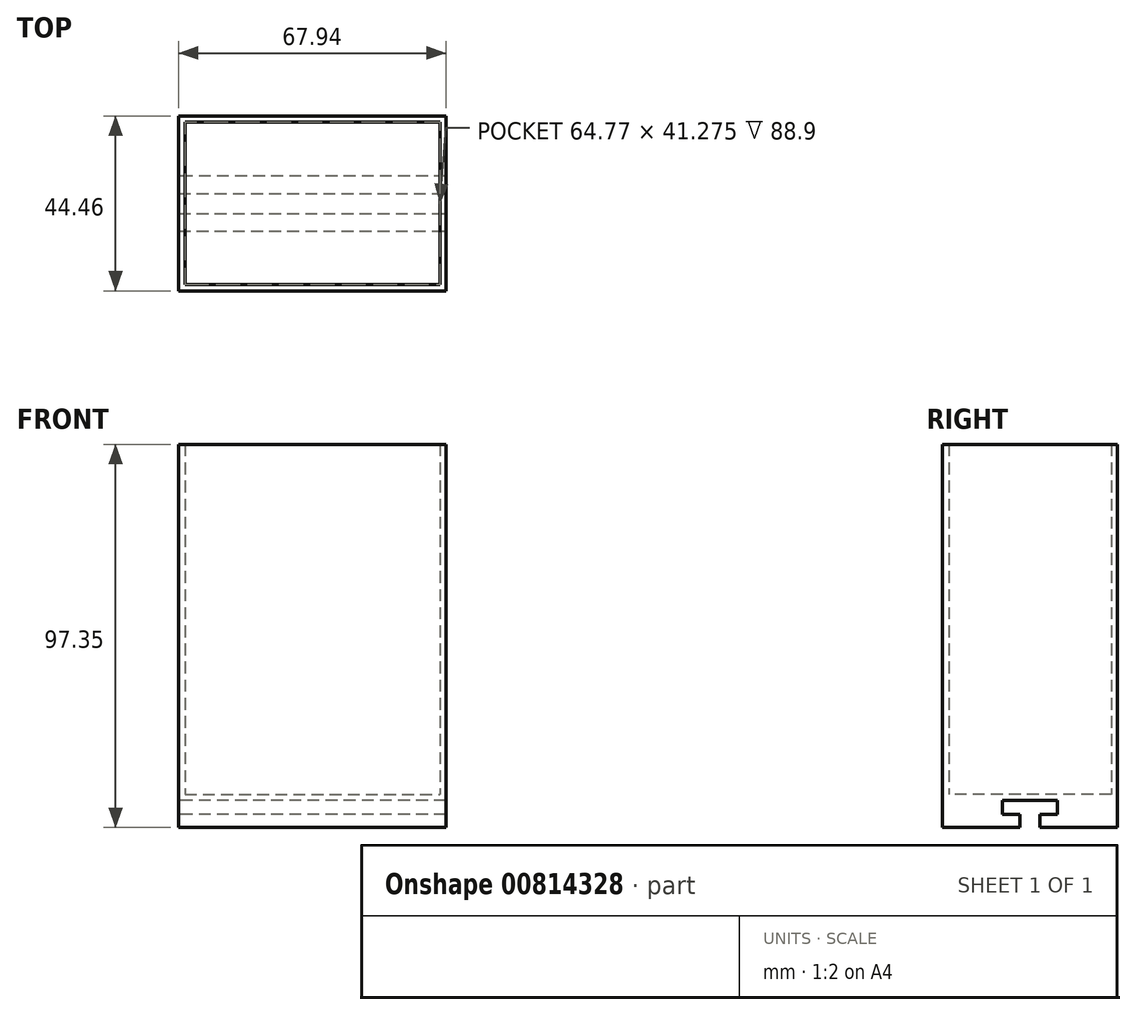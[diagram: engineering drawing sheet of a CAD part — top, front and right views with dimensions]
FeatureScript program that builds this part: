
annotation { "Feature Type Name" : "Feature", "Feature Type Description" : "" }
export const myFeature = defineFeature(function(context is Context, id is Id, definition is map)
    precondition{}
    {
        {
            var Q0;
            Q0=qCreatedBy(makeId("Top.planeOp"),FACE);
            var sketch = newSketch(context, id + "F0", { "sketchPlane" : qUnion([Q0])});
            skLineSegment(sketch, "E0.bottom", {"start": v(-33.97, 22.23) * mm, "end": v(33.97, 22.23) * mm});
            skLineSegment(sketch, "E0.top", {"start": v(-33.97, -22.23) * mm, "end": v(33.97, -22.23) * mm});
            skLineSegment(sketch, "E0.left", {"start": v(-33.97, 22.23) * mm, "end": v(-33.97, -22.23) * mm});
            skLineSegment(sketch, "E0.right", {"start": v(33.97, 22.23) * mm, "end": v(33.97, -22.23) * mm});
            skLineSegment(sketch, "E1", {"start": v(-33.97, 22.23) * mm, "end": v(33.97, -22.23) * mm, "construction": true});
            skSolve(sketch);
        }
        {
            var Q0;
            Q0 = qSketchRegion(id + "F0", true);
            extrude(context, id + "F1", {"entities" : qUnion([Q0]), "depth" : 1.59 * mm, "offsetDistance" : 25.4 * mm});
        }
        {
            var Q0;
            Q0=makeQuery(id+"F1.opExtrude","CAP_FACE",FACE,{"disambiguationData":[OSD([sQuery(id+"F0.wireOp",EDGE,"E0.bottom"),sQuery(id+"F0.wireOp",EDGE,"E0.top"),sQuery(id+"F0.wireOp",EDGE,"E0.left"),sQuery(id+"F0.wireOp",EDGE,"E0.right")])],"isStart":false});
            var sketch = newSketch(context, id + "F2", { "sketchPlane" : qUnion([Q0])});
            skLineSegment(sketch, "E2.bottom", {"start": v(-33.97, 22.23) * mm, "end": v(33.97, 22.23) * mm});
            skLineSegment(sketch, "E2.top", {"start": v(-33.97, -22.23) * mm, "end": v(33.97, -22.23) * mm});
            skLineSegment(sketch, "E2.left", {"start": v(-33.97, 22.23) * mm, "end": v(-33.97, -22.23) * mm});
            skLineSegment(sketch, "E2.right", {"start": v(33.97, 22.23) * mm, "end": v(33.97, -22.23) * mm});
            skLineSegment(sketch, "E3.0", {"start": v(-32.39, 20.64) * mm, "end": v(32.39, 20.64) * mm});
            skLineSegment(sketch, "E3.1", {"start": v(-32.39, 20.64) * mm, "end": v(-32.39, -20.64) * mm});
            skLineSegment(sketch, "E3.2", {"start": v(-32.39, -20.64) * mm, "end": v(32.39, -20.64) * mm});
            skLineSegment(sketch, "E3.3", {"start": v(32.39, 20.64) * mm, "end": v(32.39, -20.64) * mm});
            skSolve(sketch);
        }
        {
            var Q0;
            Q0 = qSketchRegion(id + "F2", true);
            extrude(context, id + "F3", {"entities" : qUnion([Q0]), "operationType" : NewBodyOperationType.ADD, "depth" : 88.9 * mm, "offsetDistance" : 25.4 * mm});
        }
        {
            var Q0;
            Q0=makeQuery(id+"F1.opExtrude","CAP_FACE",FACE,{"disambiguationData":[OSD([sQuery(id+"F0.wireOp",EDGE,"E0.bottom"),sQuery(id+"F0.wireOp",EDGE,"E0.top"),sQuery(id+"F0.wireOp",EDGE,"E0.left"),sQuery(id+"F0.wireOp",EDGE,"E0.right")])],"isStart":true});
            var sketch = newSketch(context, id + "F4", { "sketchPlane" : qUnion([Q0])});
            skLineSegment(sketch, "E4.bottom", {"start": v(-33.97, 22.23) * mm, "end": v(33.97, 22.23) * mm});
            skLineSegment(sketch, "E4.top", {"start": v(-33.97, 6.98) * mm, "end": v(33.97, 6.99) * mm});
            skLineSegment(sketch, "E4.left", {"start": v(-33.97, 22.23) * mm, "end": v(-33.97, 6.98) * mm});
            skLineSegment(sketch, "E4.right", {"start": v(33.97, 22.23) * mm, "end": v(33.97, 6.99) * mm});
            skLineSegment(sketch, "E5.bottom", {"start": v(33.97, -22.23) * mm, "end": v(-33.97, -22.23) * mm});
            skLineSegment(sketch, "E5.top", {"start": v(33.97, -6.98) * mm, "end": v(-33.97, -6.99) * mm});
            skLineSegment(sketch, "E5.left", {"start": v(33.97, -22.23) * mm, "end": v(33.97, -6.98) * mm});
            skLineSegment(sketch, "E5.right", {"start": v(-33.97, -22.23) * mm, "end": v(-33.97, -6.99) * mm});
            skSolve(sketch);
        }
        {
            var Q0;
            Q0 = qSketchRegion(id + "F4", true);
            extrude(context, id + "F5", {"entities" : qUnion([Q0]), "operationType" : NewBodyOperationType.ADD, "depth" : 6.86 * mm, "offsetDistance" : 25.4 * mm});
        }
        {
            var Q0;
            Q0=makeQuery(id+"F5.opExtrude","CAP_FACE",FACE,{"disambiguationData":[OSD([sQuery(id+"F4.wireOp",EDGE,"E5.bottom"),sQuery(id+"F4.wireOp",EDGE,"E5.top"),sQuery(id+"F4.wireOp",EDGE,"E5.left"),sQuery(id+"F4.wireOp",EDGE,"E5.right")])],"isStart":false});
            var sketch = newSketch(context, id + "F6", { "sketchPlane" : qUnion([Q0])});
            skLineSegment(sketch, "E6.bottom", {"start": v(-33.97, 6.99) * mm, "end": v(33.97, 6.99) * mm});
            skLineSegment(sketch, "E6.top", {"start": v(-33.97, 2.54) * mm, "end": v(33.97, 2.54) * mm});
            skLineSegment(sketch, "E6.left", {"start": v(-33.97, 6.99) * mm, "end": v(-33.97, 2.54) * mm});
            skLineSegment(sketch, "E6.right", {"start": v(33.97, 6.99) * mm, "end": v(33.97, 2.54) * mm});
            skLineSegment(sketch, "E7.bottom", {"start": v(-33.97, -6.99) * mm, "end": v(33.97, -6.99) * mm});
            skLineSegment(sketch, "E7.top", {"start": v(-33.97, -2.54) * mm, "end": v(33.97, -2.54) * mm});
            skLineSegment(sketch, "E7.left", {"start": v(-33.97, -6.99) * mm, "end": v(-33.97, -2.54) * mm});
            skLineSegment(sketch, "E7.right", {"start": v(33.97, -6.99) * mm, "end": v(33.97, -2.54) * mm});
            skSolve(sketch);
        }
        {
            var Q0;
            Q0 = qSketchRegion(id + "F6", true);
            extrude(context, id + "F7", {"entities" : qUnion([Q0]), "operationType" : NewBodyOperationType.ADD, "oppositeDirection" : true, "depth" : 3.3 * mm, "offsetDistance" : 25.4 * mm});
        }
    });
